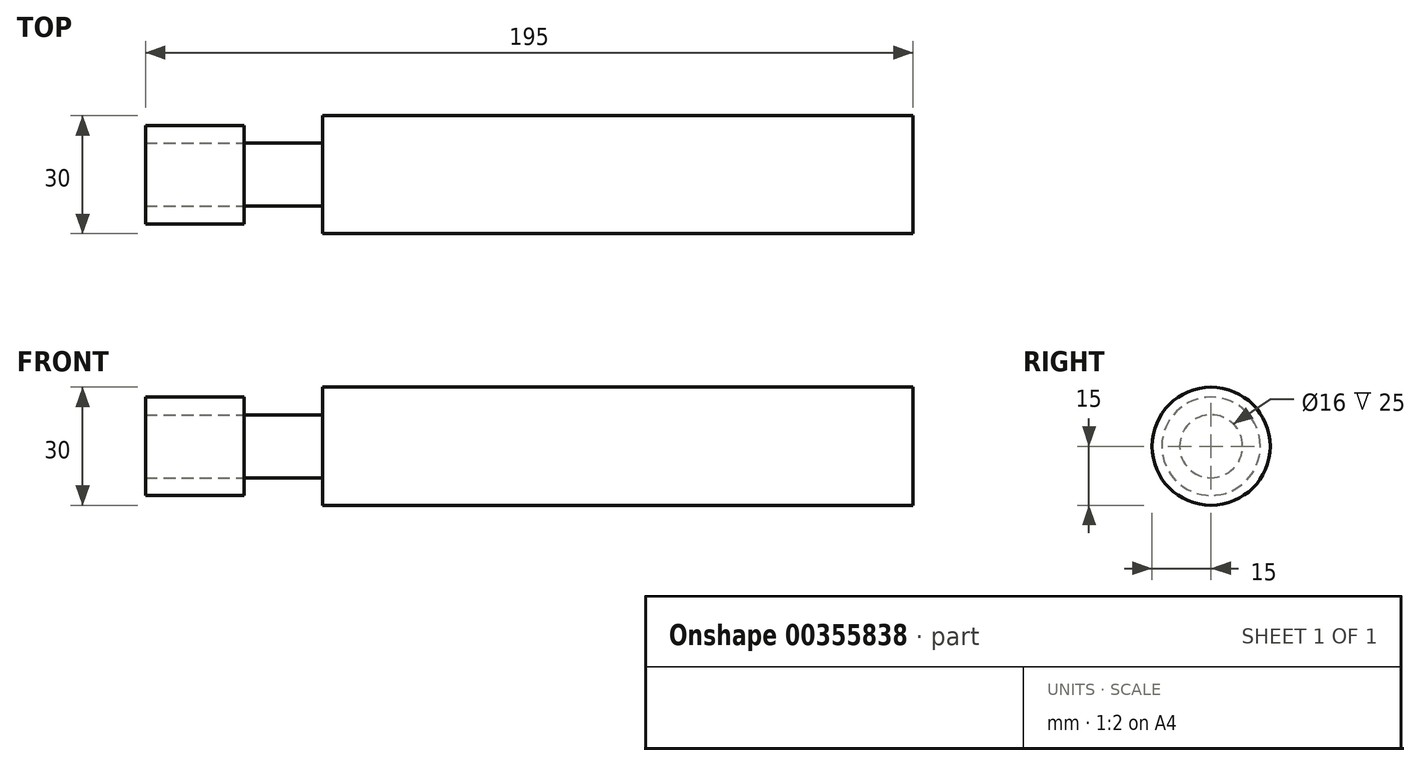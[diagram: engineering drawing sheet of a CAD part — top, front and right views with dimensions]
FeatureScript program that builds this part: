
annotation { "Feature Type Name" : "Feature", "Feature Type Description" : "" }
export const myFeature = defineFeature(function(context is Context, id is Id, definition is map)
    precondition{}
    {
        {
            var Q0;
            Q0=qCreatedBy(makeId("Top.planeOp"),FACE);
            var sketch = newSketch(context, id + "F0", { "sketchPlane" : qUnion([Q0])});
            skLineSegment(sketch, "E0", {"start": v(0, 0) * mm, "end": v(-150, 0) * mm});
            skSolve(sketch);
        }
        {
            var Q0;
            Q0=qCreatedBy(makeId("Right.planeOp"),FACE);
            var sketch = newSketch(context, id + "F1", { "sketchPlane" : qUnion([Q0])});
            skCircle(sketch, "E1", {"center": v(0, 0) * mm, "radius": 15 * mm});
            skSolve(sketch);
        }
        {
            var Q0;
            Q0=makeQuery(id+"F1.imprint","IMPRINT",FACE,{"disambiguationData":[TD([[makeQuery(id+"F1.imprint","IMPRINT",EDGE,{"derivedFrom":sQuery(id+"F1.wireOp",EDGE,"E1")}),1.0]])]});
            var Q1;
            Q1=sQuery(id+"F0.wireOp",EDGE,"E0");
            sweep(context, id + "F2", {"profiles" : qUnion([Q0]), "path" : qUnion([Q1])});
        }
        {
            var Q0;
            Q0=makeQuery(id+"F2.opSweep","CAP_FACE",FACE,{"disambiguationData":[OSD([sQuery(id+"F0.wireOp",VERTEX,"E0.end"),sQuery(id+"F1.wireOp",EDGE,"E1")])],"isStart":false});
            var sketch = newSketch(context, id + "F3", { "sketchPlane" : qUnion([Q0])});
            skCircle(sketch, "E2", {"center": v(0, 0) * mm, "radius": 8 * mm});
            skSolve(sketch);
        }
        {
            var Q0;
            Q0=makeQuery(id+"F3.imprint","IMPRINT",FACE,{"disambiguationData":[TD([[makeQuery(id+"F3.imprint","IMPRINT",EDGE,{"derivedFrom":sQuery(id+"F3.wireOp",EDGE,"E2")}),1.0]])]});
            extrude(context, id + "F4", {"entities" : qUnion([Q0]), "operationType" : NewBodyOperationType.ADD, "depth" : 20 * mm});
        }
        {
            var Q0;
            Q0=makeQuery(id+"F4.opExtrude","CAP_FACE",FACE,{"disambiguationData":[OSD([sQuery(id+"F3.wireOp",EDGE,"E2")])],"isStart":false});
            var sketch = newSketch(context, id + "F5", { "sketchPlane" : qUnion([Q0])});
            skCircle(sketch, "E3", {"center": v(0, 0) * mm, "radius": 12.5 * mm});
            skSolve(sketch);
        }
        {
            var Q0;
            Q0=makeQuery(id+"F5.imprint","IMPRINT",FACE,{"disambiguationData":[TD([[makeQuery(id+"F5.imprint","IMPRINT",EDGE,{"derivedFrom":sQuery(id+"F5.wireOp",EDGE,"E3")}),1.0]])]});
            var Q1;
            Q1=sQuery(id+"F5.wireOp",EDGE,"E3");
            extrude(context, id + "F6", {"entities" : qUnion([Q0]), "surfaceEntities" : qUnion([Q1]), "depth" : 25 * mm});
        }
        {
            var Q0;
            Q0=makeQuery(id+"F4.opExtrude","CAP_FACE",FACE,{"disambiguationData":[OSD([sQuery(id+"F3.wireOp",EDGE,"E2")])],"isStart":false});
            extrude(context, id + "F7", {"entities" : qUnion([Q0]), "depth" : 25 * mm});
        }
    });
